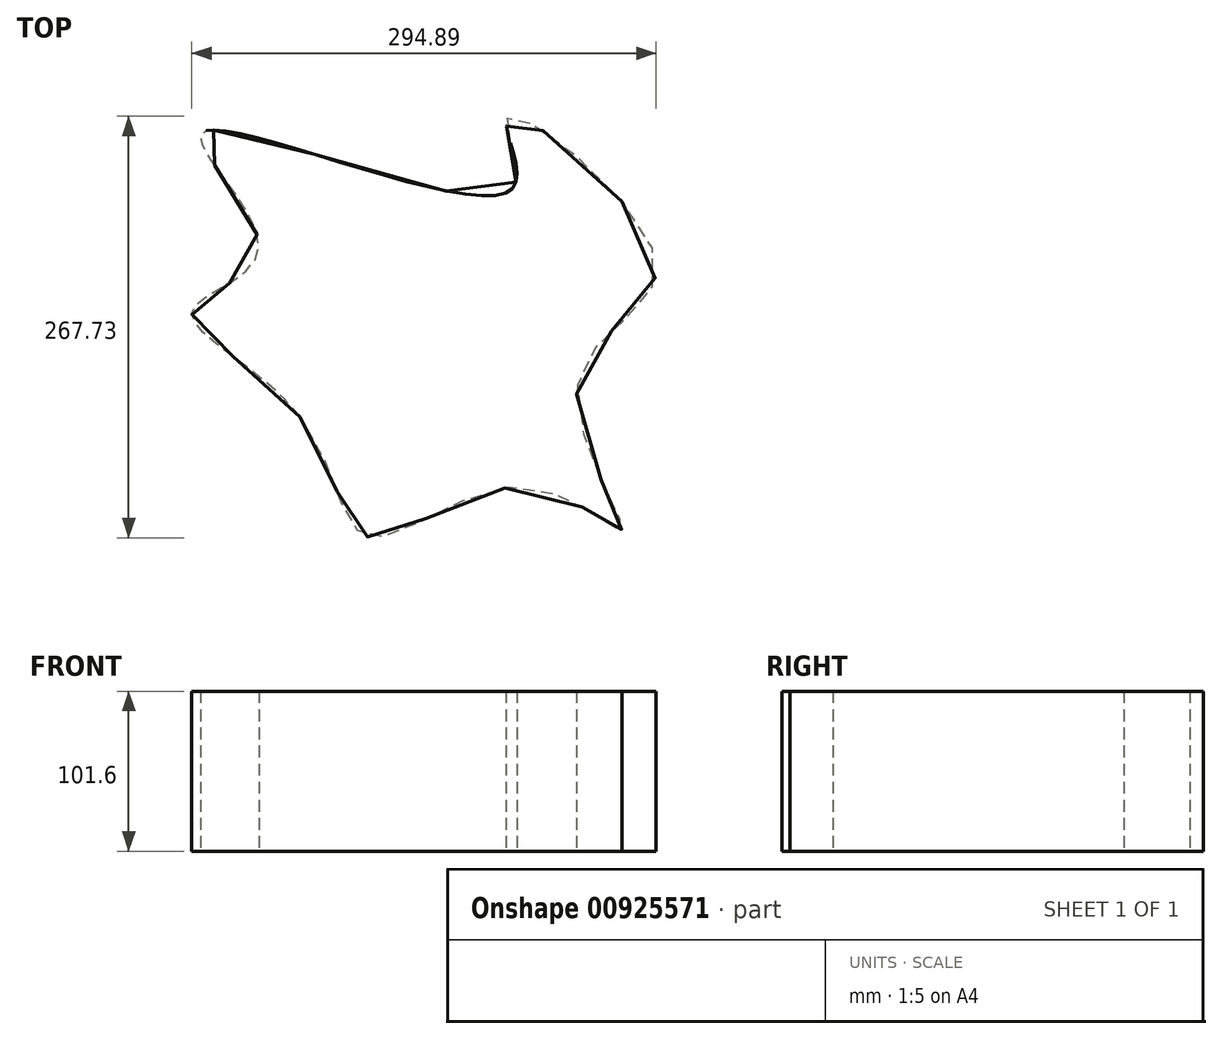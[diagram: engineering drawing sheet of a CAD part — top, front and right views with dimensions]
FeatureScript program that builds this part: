
annotation { "Feature Type Name" : "Feature", "Feature Type Description" : "" }
export const myFeature = defineFeature(function(context is Context, id is Id, definition is map)
    precondition{}
    {
        {
            var Q0;
            Q0=qCreatedBy(makeId("Top.planeOp"),FACE);
            var sketch = newSketch(context, id + "F0", { "sketchPlane" : qUnion([Q0])});
            skFitSpline(sketch, "E0", {"points": [v(-39.15, -97.98) * mm, v(-107.64, -30.14) * mm, v(-65.45, 9.1) * mm, v(-100.96, 82.76) * mm, v(94.81, 46.27) * mm, v(92.7, 92.14) * mm, v(186.61, 0) * mm, v(137.32, -74.57) * mm, v(165.12, -169.2) * mm, v(103.9, -142.6) * mm, v(4.54, -174.36) * mm, v(-39.15, -97.98) * mm]});
            skSolve(sketch);
        }
        {
            var Q0;
            Q0=qSketchRegion(id+"F0",true);
            extrude(context, id + "F1", {"entities" : qUnion([Q0]), "depth" : 203.2 * mm, "offsetDistance" : 25.4 * mm, "hasSecondDirection" : true, "secondDirectionOppositeDirection" : false, "secondDirectionDepth" : 101.6 * mm});
        }
    });
